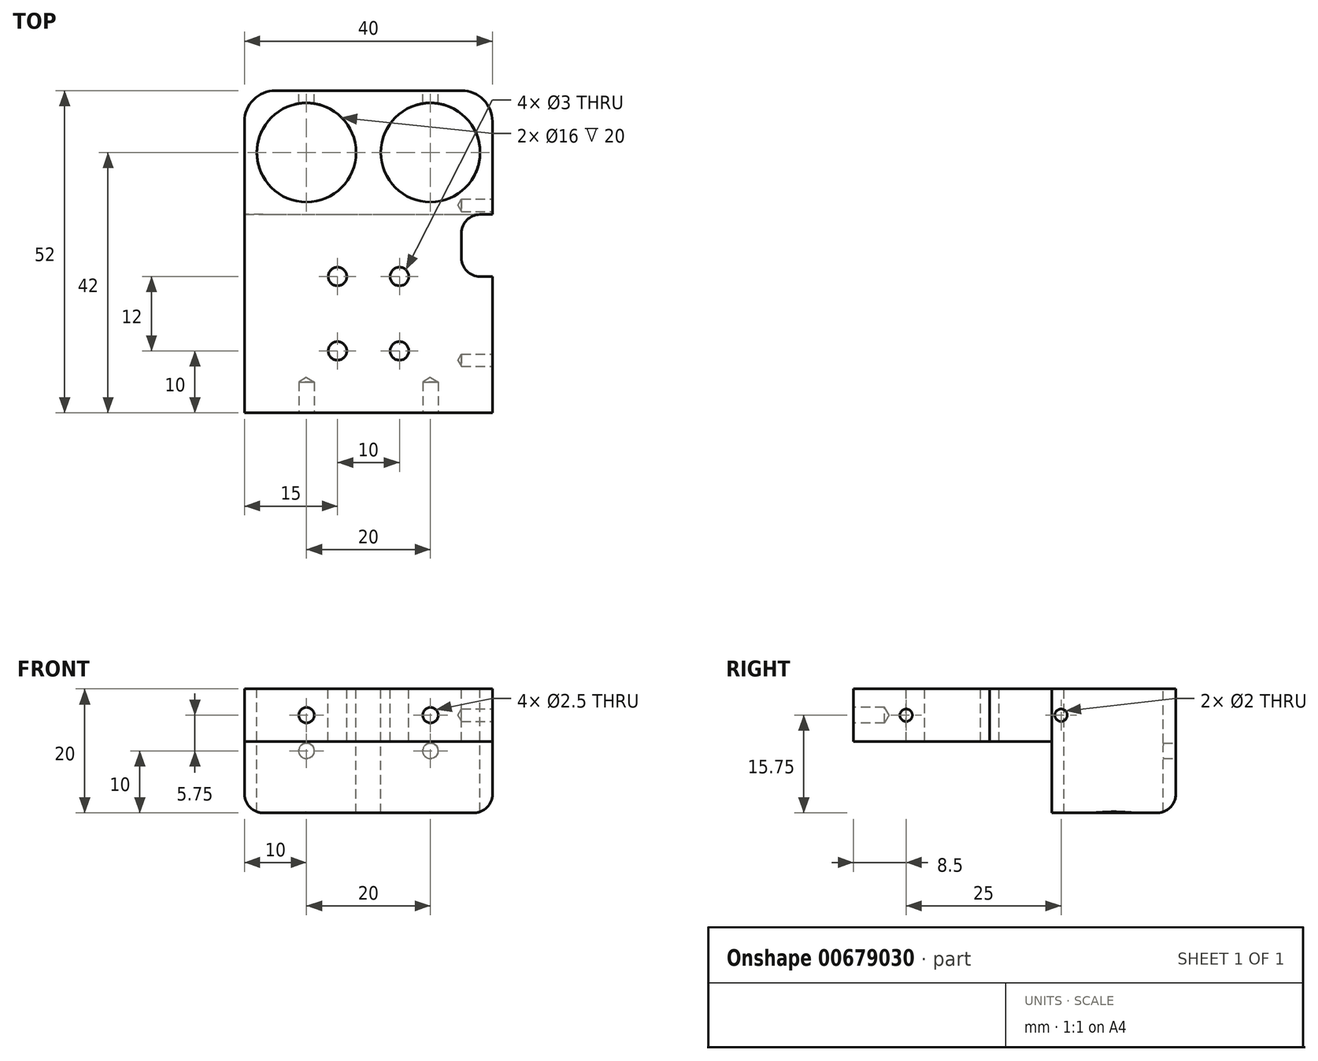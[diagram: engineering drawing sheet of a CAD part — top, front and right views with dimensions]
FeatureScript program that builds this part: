
annotation { "Feature Type Name" : "Feature", "Feature Type Description" : "" }
export const myFeature = defineFeature(function(context is Context, id is Id, definition is map)
    precondition{}
    {
        {
            var Q0;
            Q0=qCreatedBy(makeId("Top.planeOp"),FACE);
            var sketch = newSketch(context, id + "F0", { "sketchPlane" : qUnion([Q0])});
            skPoint(sketch, "E0", {"position": v(0, 0) * mm});
            skPoint(sketch, "E1", {"position": v(10, 0) * mm});
            skLineSegment(sketch, "E2", {"start": v(-15, 30) * mm, "end": v(25, 30) * mm});
            skLineSegment(sketch, "E3", {"start": v(25, 30) * mm, "end": v(25, -22) * mm});
            skLineSegment(sketch, "E4", {"start": v(25, -22) * mm, "end": v(-15, -22) * mm});
            skLineSegment(sketch, "E5", {"start": v(-15, -22) * mm, "end": v(-15, 30) * mm});
            skPoint(sketch, "E6", {"position": v(0, -12) * mm});
            skPoint(sketch, "E7", {"position": v(10, -12) * mm});
            skPoint(sketch, "E8", {"position": v(5, 0) * mm});
            skLineSegment(sketch, "E9", {"start": v(5, 0) * mm, "end": v(5, 30) * mm});
            skPoint(sketch, "E10", {"position": v(15, 20) * mm});
            skPoint(sketch, "E11", {"position": v(-5, 20) * mm});
            skLineSegment(sketch, "E12", {"start": v(25, 10) * mm, "end": v(-15, 10) * mm});
            skSolve(sketch);
        }
        {
            var Q0;
            Q0=makeQuery(id+"F0.imprint","IMPRINT",FACE,{"disambiguationData":[TD([[makeQuery(id+"F0.imprint","IMPRINT",EDGE,{"derivedFrom":sQuery(id+"F0.wireOp",EDGE,"E2")}),-1.0]])]});
            var Q1;
            {var subQ1=sQuery(id+"F0.wireOp",EDGE,"E4");Q1=makeQuery(id+"F0.imprint","IMPRINT",FACE,{"disambiguationData":[TD([[makeQuery(id+"F0.imprint","IMPRINT",EDGE,{"derivedFrom":subQ1}),-1.0]])]});}
            extrude(context, id + "F1", {"entities" : qUnion([Q0, Q1]), "oppositeDirection" : true, "depth" : 20 * mm, "offsetDistance" : 25 * mm});
        }
        {
            var Q0;
            Q0=sQuery(id+"F0.wireOp",VERTEX,"E1");
            var Q1;
            Q1=sQuery(id+"F0.wireOp",VERTEX,"E0");
            var Q2;
            Q2=sQuery(id+"F0.wireOp",VERTEX,"E6");
            var Q3;
            Q3=sQuery(id+"F0.wireOp",VERTEX,"E7");
            var Q4;
            Q4=makeQuery(id+"F1.opExtrude","SWEPT_BODY",BODY,{"disambiguationData":[OSD([sQuery(id+"F0.wireOp",EDGE,"E2"),sQuery(id+"F0.wireOp",EDGE,"E3"),sQuery(id+"F0.wireOp",EDGE,"E4"),sQuery(id+"F0.wireOp",EDGE,"E5")])]});
            hole(context, id + "F2", {"style" : HoleStyle.SIMPLE, "endStyle" : HoleEndStyle.BLIND, "holeDiameter" : 3 * mm, "majorDiameter" : 5 * mm, "holeDepth" : 20 * mm, "isTappedThrough" : true, "tappedDepth" : 12 * mm, "tapClearance" : 3, "startFromSketch" : true, "locations" : qUnion([Q0, Q1, Q2, Q3]), "scope" : qUnion([Q4])});
        }
        {
            var Q0;
            Q0=sQuery(id+"F0.wireOp",VERTEX,"E10");
            var Q1;
            Q1=sQuery(id+"F0.wireOp",VERTEX,"E11");
            var Q2;
            Q2=makeQuery(id+"F1.opExtrude","SWEPT_BODY",BODY,{"disambiguationData":[OSD([sQuery(id+"F0.wireOp",EDGE,"E2"),sQuery(id+"F0.wireOp",EDGE,"E3"),sQuery(id+"F0.wireOp",EDGE,"E4"),sQuery(id+"F0.wireOp",EDGE,"E5")])]});
            hole(context, id + "F3", {"style" : HoleStyle.SIMPLE, "endStyle" : HoleEndStyle.BLIND, "holeDiameter" : 16 * mm, "majorDiameter" : 5 * mm, "holeDepth" : 20 * mm, "isTappedThrough" : true, "tappedDepth" : 12 * mm, "tapClearance" : 3, "startFromSketch" : true, "locations" : qUnion([Q0, Q1]), "scope" : qUnion([Q2])});
        }
        {
            var Q0;
            Q0=makeQuery(id+"F1.opExtrude","CAP_FACE",FACE,{"disambiguationData":[OSD([sQuery(id+"F0.wireOp",EDGE,"E2"),sQuery(id+"F0.wireOp",EDGE,"E3"),sQuery(id+"F0.wireOp",EDGE,"E4"),sQuery(id+"F0.wireOp",EDGE,"E5")])],"isStart":false});
            var sketch = newSketch(context, id + "F4", { "sketchPlane" : qUnion([Q0])});
            skLineSegment(sketch, "E13.bottom", {"start": v(-15, 22) * mm, "end": v(25, 22) * mm});
            skLineSegment(sketch, "E13.top", {"start": v(-15, -10) * mm, "end": v(25, -10) * mm});
            skLineSegment(sketch, "E13.left", {"start": v(-15, 22) * mm, "end": v(-15, -10) * mm});
            skLineSegment(sketch, "E13.right", {"start": v(25, 22) * mm, "end": v(25, -10) * mm});
            skSolve(sketch);
        }
        {
            var Q0;
            Q0=makeQuery(id+"F4.imprint","IMPRINT",FACE,{"disambiguationData":[TD([[makeQuery(id+"F4.imprint","IMPRINT",EDGE,{"derivedFrom":sQuery(id+"F4.wireOp",EDGE,"E13.bottom")}),1.0]])]});
            extrude(context, id + "F5", {"entities" : qUnion([Q0]), "operationType" : NewBodyOperationType.REMOVE, "oppositeDirection" : true, "depth" : 11.5 * mm, "offsetDistance" : 25 * mm});
        }
        {
            var Q0;
            Q0=makeQuery(id+"F1.opExtrude","SWEPT_FACE",FACE,{"disambiguationData":[OSD([sQuery(id+"F0.wireOp",EDGE,"E4")])]});
            var sketch = newSketch(context, id + "F6", { "sketchPlane" : qUnion([Q0])});
            skLineSegment(sketch, "E14", {"start": v(5, 0) * mm, "end": v(5, -8.5) * mm});
            skPoint(sketch, "E15", {"position": v(-5, -4.25) * mm});
            skPoint(sketch, "E15.positionSnap0", {"position": v(5, -4.25) * mm});
            skPoint(sketch, "E16", {"position": v(15, -4.25) * mm});
            skSolve(sketch);
        }
        {
            var Q0;
            Q0=sQuery(id+"F6.wireOp",VERTEX,"E15");
            var Q1;
            Q1=sQuery(id+"F6.wireOp",VERTEX,"E16");
            var Q2;
            Q2=makeQuery(id+"F1.opExtrude","SWEPT_BODY",BODY,{"disambiguationData":[OSD([sQuery(id+"F0.wireOp",EDGE,"E2"),sQuery(id+"F0.wireOp",EDGE,"E3"),sQuery(id+"F0.wireOp",EDGE,"E4"),sQuery(id+"F0.wireOp",EDGE,"E5")])]});
            hole(context, id + "F7", {"style" : HoleStyle.SIMPLE, "endStyle" : HoleEndStyle.BLIND, "holeDiameter" : 2.5 * mm, "majorDiameter" : 5 * mm, "holeDepth" : 5 * mm, "isTappedThrough" : true, "tappedDepth" : 12 * mm, "tapClearance" : 3, "startFromSketch" : true, "locations" : qUnion([Q0, Q1]), "scope" : qUnion([Q2])});
        }
        {
            var Q0;
            Q0=makeQuery(id+"F1.opExtrude","SWEPT_EDGE",EDGE,{"disambiguationData":[OSD([sQuery(id+"F0.wireOp",EDGE,"E2"),sQuery(id+"F0.wireOp",EDGE,"E5")])]});
            var Q1;
            Q1=makeQuery(id+"F1.opExtrude","SWEPT_EDGE",EDGE,{"disambiguationData":[OSD([sQuery(id+"F0.wireOp",EDGE,"E2"),sQuery(id+"F0.wireOp",EDGE,"E3")])]});
            fillet(context, id + "F8", {"entities" : qUnion([Q0, Q1]), "radius" : 5 * mm, "tangentPropagation" : true, "allowEdgeOverflow" : false});
        }
        {
            var Q0;
            Q0=makeQuery(id+"F1.opExtrude","SWEPT_FACE",FACE,{"disambiguationData":[OSD([sQuery(id+"F0.wireOp",EDGE,"E2")])]});
            var sketch = newSketch(context, id + "F9", { "sketchPlane" : qUnion([Q0])});
            skPoint(sketch, "E17", {"position": v(5, -10) * mm});
            skPoint(sketch, "E18", {"position": v(-15, -10) * mm});
            skLineSegment(sketch, "E19", {"start": v(-5, 0) * mm, "end": v(-5, -20) * mm});
            skSolve(sketch);
        }
        {
            var Q0;
            Q0=sQuery(id+"F9.wireOp",VERTEX,"E17");
            var Q1;
            Q1=sQuery(id+"F9.wireOp",VERTEX,"E18");
            var Q2;
            Q2=makeQuery(id+"F1.opExtrude","SWEPT_BODY",BODY,{"disambiguationData":[OSD([sQuery(id+"F0.wireOp",EDGE,"E2"),sQuery(id+"F0.wireOp",EDGE,"E3"),sQuery(id+"F0.wireOp",EDGE,"E4"),sQuery(id+"F0.wireOp",EDGE,"E5")])]});
            hole(context, id + "F10", {"style" : HoleStyle.SIMPLE, "endStyle" : HoleEndStyle.BLIND, "holeDiameter" : 2.5 * mm, "majorDiameter" : 5 * mm, "holeDepth" : 5 * mm, "isTappedThrough" : true, "tappedDepth" : 12 * mm, "tapClearance" : 3, "startFromSketch" : true, "locations" : qUnion([Q0, Q1]), "scope" : qUnion([Q2])});
        }
        {
            var Q0;
            Q0=makeQuery(id+"F1.opExtrude","CAP_EDGE",EDGE,{"disambiguationData":[OSD([sQuery(id+"F0.wireOp",EDGE,"E5")])],"isStart":false});
            var Q1;
            Q1=makeQuery(id+"F5.boolean.opBoolean","COPY",EDGE,{"derivedFrom":makeQuery(id+"F5.opExtrude","CAP_EDGE",EDGE,{"disambiguationData":[OSD([sQuery(id+"F4.wireOp",EDGE,"E13.top")])],"isStart":true})});
            fillet(context, id + "F11", {"entities" : qUnion([Q0, Q1]), "radius" : 3 * mm, "tangentPropagation" : true, "allowEdgeOverflow" : false});
        }
        {
            var Q0;
            Q0=makeQuery(id+"F1.opExtrude","SWEPT_FACE",FACE,{"disambiguationData":[OSD([sQuery(id+"F0.wireOp",EDGE,"E3")])]});
            var sketch = newSketch(context, id + "F12", { "sketchPlane" : qUnion([Q0])});
            skLineSegment(sketch, "E20", {"start": v(-22, -4.25) * mm, "end": v(25, -4.25) * mm});
            skPoint(sketch, "E21", {"position": v(-13.5, -4.25) * mm});
            skPoint(sketch, "E22", {"position": v(11.5, -4.25) * mm});
            skSolve(sketch);
        }
        {
            var Q0;
            {var subQ1=sQuery(id+"F0.wireOp",EDGE,"E4");Q0=makeQuery(id+"F0.imprint","IMPRINT",FACE,{"disambiguationData":[TD([[makeQuery(id+"F0.imprint","IMPRINT",EDGE,{"derivedFrom":subQ1}),-1.0]])]});}
            var sketch = newSketch(context, id + "F13", { "sketchPlane" : qUnion([Q0])});
            skLineSegment(sketch, "E23.bottom", {"start": v(25, 10) * mm, "end": v(20, 10) * mm});
            skLineSegment(sketch, "E23.top", {"start": v(25, 0) * mm, "end": v(20, 0) * mm});
            skLineSegment(sketch, "E23.left", {"start": v(25, 10) * mm, "end": v(25, 0) * mm});
            skLineSegment(sketch, "E23.right", {"start": v(20, 10) * mm, "end": v(20, 0) * mm});
            skSolve(sketch);
        }
        {
            var Q0;
            Q0=makeQuery(id+"F13.imprint","IMPRINT",FACE,{"disambiguationData":[TD([[makeQuery(id+"F13.imprint","IMPRINT",EDGE,{"derivedFrom":sQuery(id+"F13.wireOp",EDGE,"E23.bottom")}),1.0]])]});
            extrude(context, id + "F14", {"entities" : qUnion([Q0]), "operationType" : NewBodyOperationType.REMOVE, "oppositeDirection" : true, "depth" : 25 * mm, "offsetDistance" : 25 * mm});
        }
        {
            var Q0;
            Q0=makeQuery(id+"F14.boolean.opBoolean","COPY",EDGE,{"derivedFrom":makeQuery(id+"F14.opExtrude","SWEPT_EDGE",EDGE,{"disambiguationData":[OSD([sQuery(id+"F0.wireOp",EDGE,"E12"),sQuery(id+"F13.wireOp",EDGE,"E23.bottom"),sQuery(id+"F13.wireOp",EDGE,"E23.right")])]})});
            var Q1;
            Q1=makeQuery(id+"F14.boolean.opBoolean","COPY",EDGE,{"derivedFrom":makeQuery(id+"F14.opExtrude","SWEPT_EDGE",EDGE,{"disambiguationData":[OSD([sQuery(id+"F13.wireOp",EDGE,"E23.top"),sQuery(id+"F13.wireOp",EDGE,"E23.right")])]})});
            fillet(context, id + "F15", {"entities" : qUnion([Q0, Q1]), "radius" : 3 * mm, "tangentPropagation" : true, "allowEdgeOverflow" : false});
        }
        {
            var Q0;
            Q0=sQuery(id+"F12.wireOp",VERTEX,"E21");
            var Q1;
            Q1=sQuery(id+"F12.wireOp",VERTEX,"E22");
            var Q2;
            Q2=makeQuery(id+"F1.opExtrude","SWEPT_BODY",BODY,{"disambiguationData":[OSD([sQuery(id+"F0.wireOp",EDGE,"E2"),sQuery(id+"F0.wireOp",EDGE,"E3"),sQuery(id+"F0.wireOp",EDGE,"E4"),sQuery(id+"F0.wireOp",EDGE,"E5")])]});
            hole(context, id + "F16", {"style" : HoleStyle.SIMPLE, "endStyle" : HoleEndStyle.BLIND, "holeDiameter" : 2 * mm, "majorDiameter" : 5 * mm, "holeDepth" : 5 * mm, "isTappedThrough" : true, "tappedDepth" : 12 * mm, "tapClearance" : 3, "startFromSketch" : true, "locations" : qUnion([Q0, Q1]), "scope" : qUnion([Q2])});
        }
    });
